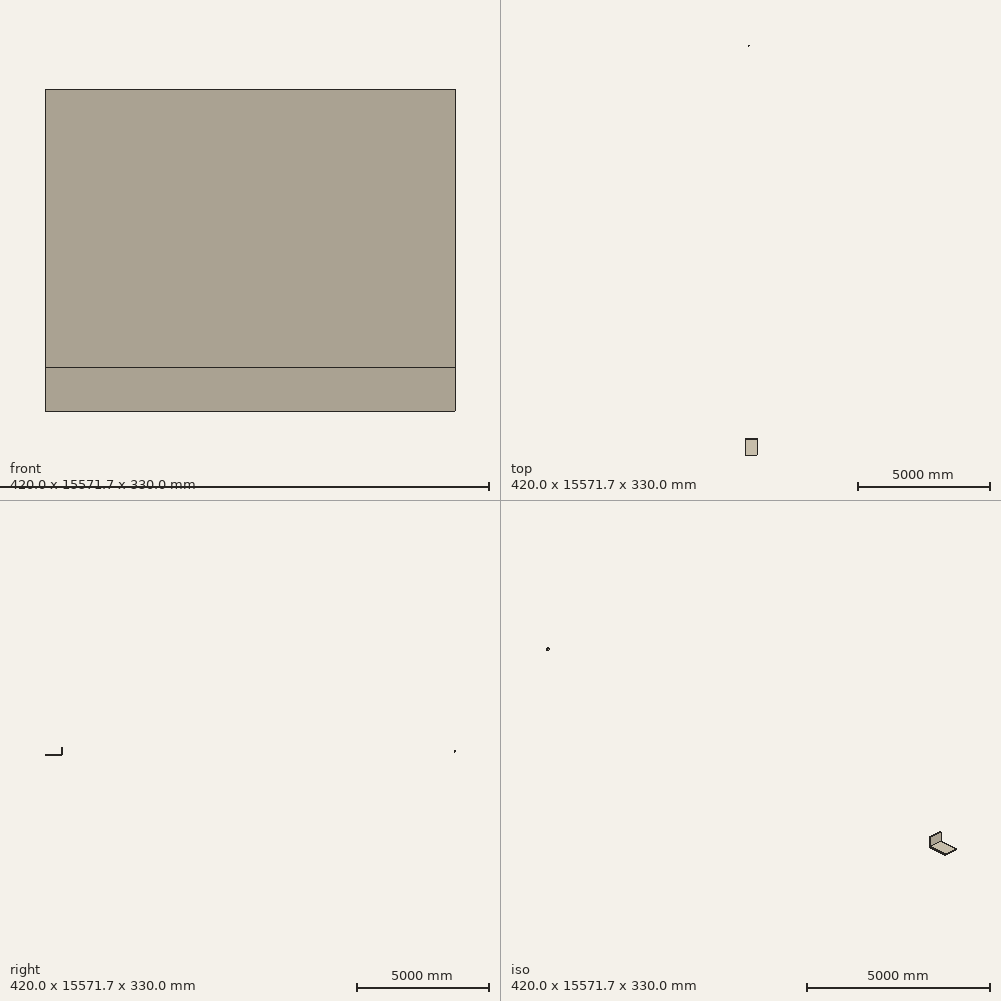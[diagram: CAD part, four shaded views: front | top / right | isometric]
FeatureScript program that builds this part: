
annotation { "Feature Type Name" : "Feature", "Feature Type Description" : "" }
export const myFeature = defineFeature(function(context is Context, id is Id, definition is map)
    precondition{}
    {
        {
            var Q0;
            Q0=qCreatedBy(makeId("Top.planeOp"),FACE);
            var sketch = newSketch(context, id + "F0", { "sketchPlane" : qUnion([Q0])});
            skLineSegment(sketch, "E0.bottom", {"start": v(-79.11, -15719.36) * mm, "end": v(340.89, -15719.36) * mm});
            skLineSegment(sketch, "E0.top", {"start": v(-79.11, -15084.36) * mm, "end": v(340.89, -15084.36) * mm});
            skLineSegment(sketch, "E0.left", {"start": v(-79.11, -15719.36) * mm, "end": v(-79.11, -15084.36) * mm});
            skLineSegment(sketch, "E0.right", {"start": v(340.89, -15719.36) * mm, "end": v(340.89, -15084.36) * mm});
            skSolve(sketch);
        }
        {
            var Q0;
            Q0=makeQuery(id+"F0.imprint","IMPRINT",FACE,{"disambiguationData":[TD([[makeQuery(id+"F0.imprint","IMPRINT",EDGE,{"derivedFrom":sQuery(id+"F0.wireOp",EDGE,"E0.bottom")}),1.0]])]});
            extrude(context, id + "F1", {"entities" : qUnion([Q0]), "depth" : 45 * mm, "offsetDistance" : 25 * mm});
        }
        {
            var Q0;
            Q0=makeQuery(id+"F1.opExtrude","CAP_FACE",FACE,{"disambiguationData":[OSD([sQuery(id+"F0.wireOp",EDGE,"E0.bottom"),sQuery(id+"F0.wireOp",EDGE,"E0.top"),sQuery(id+"F0.wireOp",EDGE,"E0.left"),sQuery(id+"F0.wireOp",EDGE,"E0.right")])],"isStart":false});
            var sketch = newSketch(context, id + "F2", { "sketchPlane" : qUnion([Q0])});
            skLineSegment(sketch, "E1.bottom", {"start": v(-79.11, -15084.36) * mm, "end": v(340.89, -15084.36) * mm});
            skLineSegment(sketch, "E1.top", {"start": v(-79.11, -15129.36) * mm, "end": v(340.89, -15129.36) * mm});
            skLineSegment(sketch, "E1.left", {"start": v(-79.11, -15084.36) * mm, "end": v(-79.11, -15129.36) * mm});
            skLineSegment(sketch, "E1.right", {"start": v(340.89, -15084.36) * mm, "end": v(340.89, -15129.36) * mm});
            skSolve(sketch);
        }
        {
            var Q0;
            Q0 = qSketchRegion(id + "F2", true);
            extrude(context, id + "F3", {"entities" : qUnion([Q0]), "depth" : (365 - 80) * mm, "offsetDistance" : 25 * mm});
        }
        {
            var Q0;
            Q0=qCreatedBy(makeId("Right.planeOp"),FACE);
            var sketch = newSketch(context, id + "F4", { "sketchPlane" : qUnion([Q0])});
            skLineSegment(sketch, "E2.bottom", {"start": v(-197.7, 165.35) * mm, "end": v(-147.7, 165.35) * mm});
            skLineSegment(sketch, "E2.top", {"start": v(-197.7, 115.35) * mm, "end": v(-147.7, 115.35) * mm});
            skLineSegment(sketch, "E2.left", {"start": v(-197.7, 165.35) * mm, "end": v(-197.7, 115.35) * mm});
            skLineSegment(sketch, "E2.right", {"start": v(-147.7, 165.35) * mm, "end": v(-147.7, 115.35) * mm});
            skSolve(sketch);
        }
        {
            var Q0;
            Q0 = qSketchRegion(id + "F4", true);
            extrude(context, id + "F5", {"entities" : qUnion([Q0]), "depth" : 50 * mm, "offsetDistance" : 25 * mm});
        }
        {
            var Q0;
            Q0=makeQuery(id+"F5.opExtrude","SWEPT_FACE",FACE,{"disambiguationData":[OSD([sQuery(id+"F4.wireOp",EDGE,"E2.bottom")])]});
            var sketch = newSketch(context, id + "F6", { "sketchPlane" : qUnion([Q0])});
            skLineSegment(sketch, "E3.bottom", {"start": v(15, -182.7) * mm, "end": v(35, -182.7) * mm});
            skLineSegment(sketch, "E3.top", {"start": v(15, -162.7) * mm, "end": v(35, -162.7) * mm});
            skLineSegment(sketch, "E3.left", {"start": v(15, -182.7) * mm, "end": v(15, -162.7) * mm});
            skLineSegment(sketch, "E3.right", {"start": v(35, -182.7) * mm, "end": v(35, -162.7) * mm});
            skPoint(sketch, "E3.middle", {"position": v(25, -172.7) * mm});
            skPoint(sketch, "E3.middle.positionSnap0", {"position": v(25, -147.7) * mm});
            skPoint(sketch, "E3.middle.positionSnap1", {"position": v(50, -172.7) * mm});
            skPoint(sketch, "E3.centerSnap0", {"position": v(25, -147.7) * mm});
            skPoint(sketch, "E3.centerSnap1", {"position": v(50, -172.7) * mm});
            skSolve(sketch);
        }
        {
            var Q0;
            Q0 = qSketchRegion(id + "F6", true);
            extrude(context, id + "F7", {"entities" : qUnion([Q0]), "operationType" : NewBodyOperationType.ADD, "depth" : 35 * mm, "offsetDistance" : 25 * mm});
        }
    });
